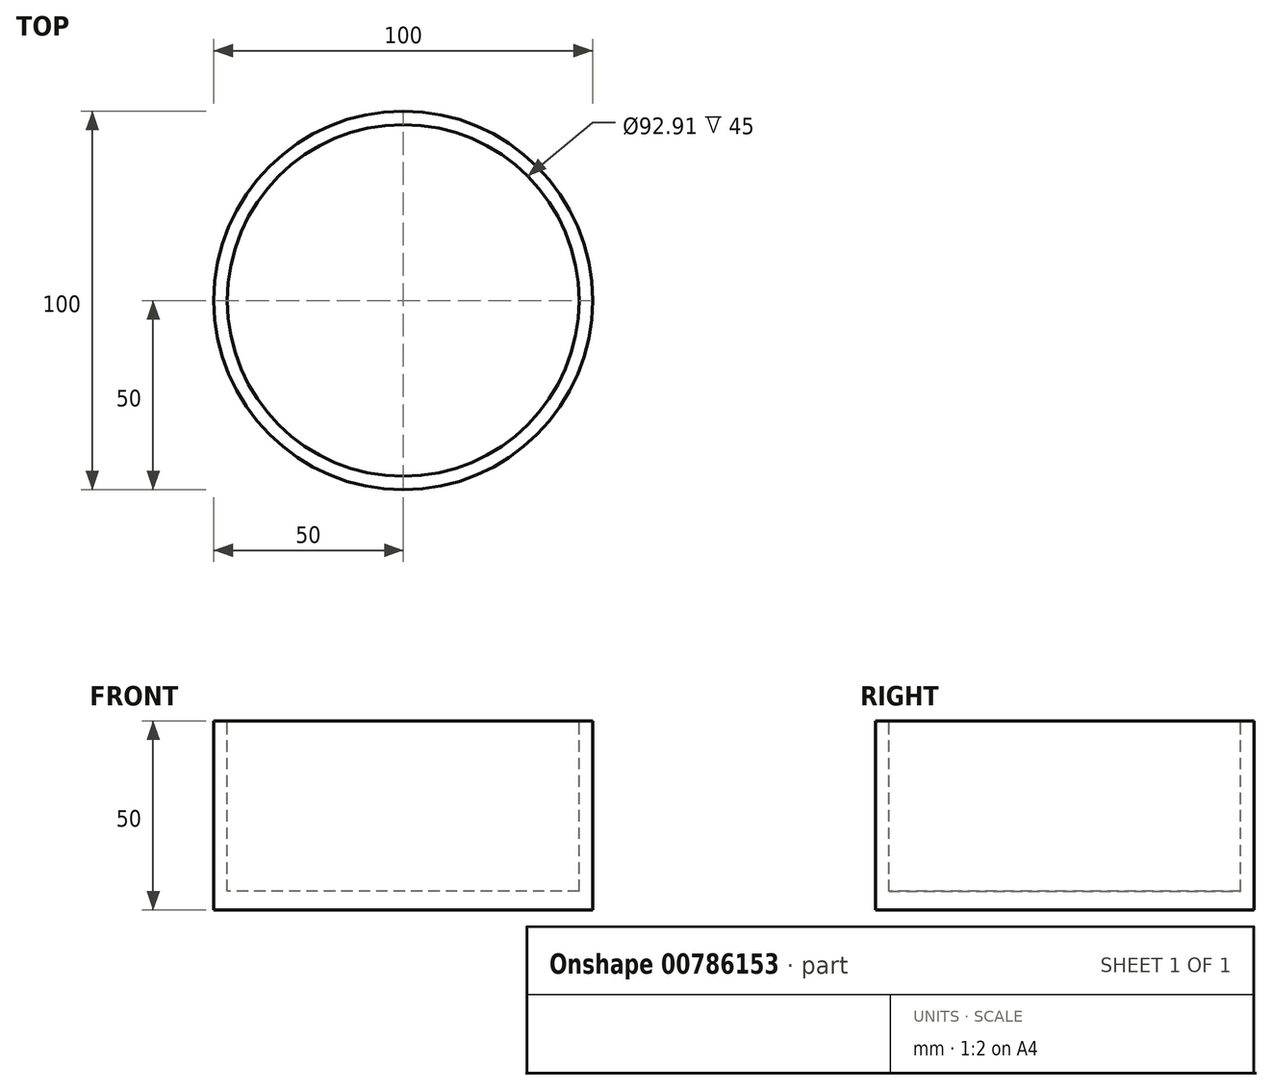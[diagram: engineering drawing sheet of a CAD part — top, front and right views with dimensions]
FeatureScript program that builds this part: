
annotation { "Feature Type Name" : "Feature", "Feature Type Description" : "" }
export const myFeature = defineFeature(function(context is Context, id is Id, definition is map)
    precondition{}
    {
        {
            var Q0;
            Q0=qCreatedBy(makeId("Top.planeOp"),FACE);
            var sketch = newSketch(context, id + "F0", { "sketchPlane" : qUnion([Q0])});
            skCircle(sketch, "E0", {"center": v(0, 0) * mm, "radius": 50 * mm});
            skSolve(sketch);
        }
        {
            var Q0;
            Q0=makeQuery(id+"F0.imprint","IMPRINT",FACE,{"disambiguationData":[TD([[makeQuery(id+"F0.imprint","IMPRINT",EDGE,{"derivedFrom":sQuery(id+"F0.wireOp",EDGE,"E0")}),1.0]])]});
            extrude(context, id + "F1", {"entities" : qUnion([Q0]), "oppositeDirection" : true, "depth" : 50 * mm, "offsetDistance" : 25 * mm});
        }
        {
            var Q0;
            Q0=makeQuery(id+"F1.opExtrude","CAP_FACE",FACE,{"disambiguationData":[OSD([sQuery(id+"F0.wireOp",EDGE,"E0")])],"isStart":true});
            var sketch = newSketch(context, id + "F2", { "sketchPlane" : qUnion([Q0])});
            skCircle(sketch, "E1", {"center": v(0, 0) * mm, "radius": 46.45 * mm});
            skSolve(sketch);
        }
        {
            var Q0;
            Q0=makeQuery(id+"F2.imprint","IMPRINT",FACE,{"disambiguationData":[TD([[makeQuery(id+"F2.imprint","IMPRINT",EDGE,{"derivedFrom":sQuery(id+"F2.wireOp",EDGE,"E1")}),1.0]])]});
            extrude(context, id + "F3", {"entities" : qUnion([Q0]), "operationType" : NewBodyOperationType.REMOVE, "oppositeDirection" : true, "depth" : 45 * mm, "offsetDistance" : 25 * mm});
        }
    });
